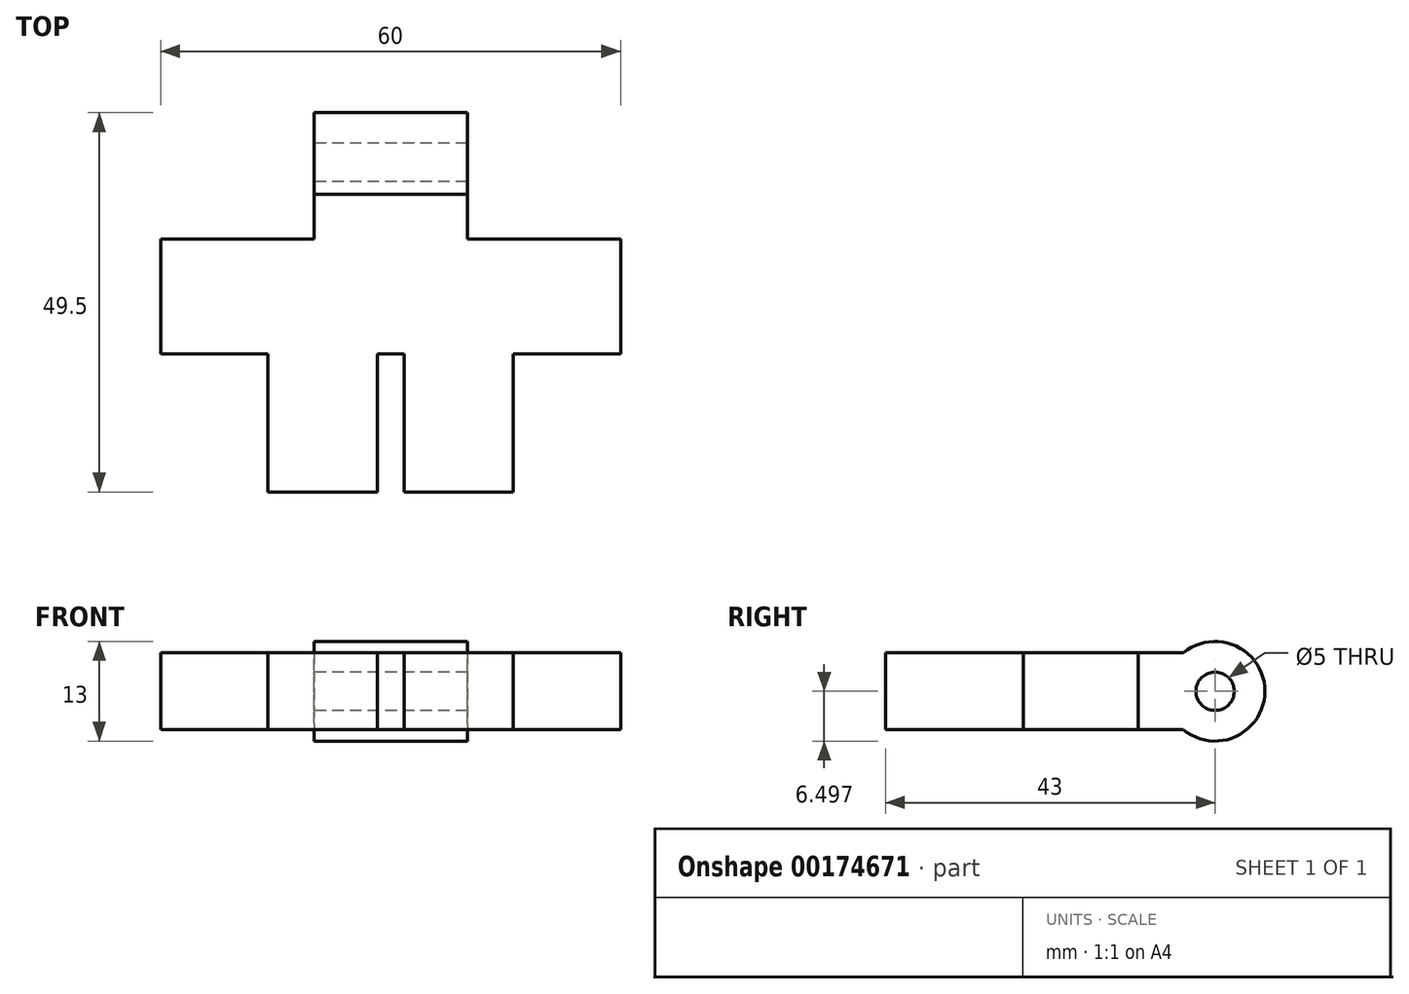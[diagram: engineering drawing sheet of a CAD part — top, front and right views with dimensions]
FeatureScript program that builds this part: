
annotation { "Feature Type Name" : "Feature", "Feature Type Description" : "" }
export const myFeature = defineFeature(function(context is Context, id is Id, definition is map)
    precondition{}
    {
        {
            var Q0;
            Q0=qCreatedBy(makeId("Top.planeOp"),FACE);
            var sketch = newSketch(context, id + "F0", { "sketchPlane" : qUnion([Q0])});
            skLineSegment(sketch, "E0", {"start": v(-30, 0) * mm, "end": v(-30, 15) * mm});
            skLineSegment(sketch, "E1", {"start": v(-30, 0) * mm, "end": v(-16, 0) * mm});
            skLineSegment(sketch, "E2", {"start": v(-16, 0) * mm, "end": v(-16, -18) * mm});
            skLineSegment(sketch, "E3", {"start": v(-16, -18) * mm, "end": v(-1.75, -18) * mm});
            skLineSegment(sketch, "E4", {"start": v(-1.75, -18) * mm, "end": v(-1.75, 0) * mm});
            skLineSegment(sketch, "E5", {"start": v(-1.75, 0) * mm, "end": v(0, 0) * mm});
            skLineSegment(sketch, "E6", {"start": v(-30, 15) * mm, "end": v(-10, 15) * mm});
            skLineSegment(sketch, "E7", {"start": v(-10, 15) * mm, "end": v(-10, 25) * mm});
            skLineSegment(sketch, "E8", {"start": v(-10, 25) * mm, "end": v(0, 25) * mm});
            skLineSegment(sketch, "E9.MirrorCS", {"start": v(10, 25) * mm, "end": v(0, 25) * mm});
            skLineSegment(sketch, "E10.MirrorCS", {"start": v(10, 15) * mm, "end": v(10, 25) * mm});
            skLineSegment(sketch, "E11.MirrorCS", {"start": v(30, 15) * mm, "end": v(10, 15) * mm});
            skLineSegment(sketch, "E12.MirrorCS", {"start": v(30, 0) * mm, "end": v(30, 15) * mm});
            skLineSegment(sketch, "E13.MirrorCS", {"start": v(30, 0) * mm, "end": v(16, 0) * mm});
            skLineSegment(sketch, "E14.MirrorCS", {"start": v(16, 0) * mm, "end": v(16, -18) * mm});
            skLineSegment(sketch, "E15.MirrorCS", {"start": v(16, -18) * mm, "end": v(1.75, -18) * mm});
            skLineSegment(sketch, "E16.MirrorCS", {"start": v(1.75, -18) * mm, "end": v(1.75, 0) * mm});
            skLineSegment(sketch, "E17.MirrorCS", {"start": v(1.75, 0) * mm, "end": v(0, 0) * mm});
            skSolve(sketch);
        }
        {
            var Q0;
            Q0 = qSketchRegion(id + "F0", true);
            extrude(context, id + "F1", {"entities" : qUnion([Q0]), "depth" : 10 * mm});
        }
        {
            var Q0;
            Q0=qCreatedBy(makeId("Right.planeOp"),FACE);
            var sketch = newSketch(context, id + "F2", { "sketchPlane" : qUnion([Q0])});
            skCircle(sketch, "E18", {"center": v(25, 5) * mm, "radius": 6.5 * mm});
            skCircle(sketch, "E19", {"center": v(25, 5) * mm, "radius": 2.5 * mm});
            skSolve(sketch);
        }
        {
            var Q0;
            Q0 = qSketchRegion(id + "F2", true);
            extrude(context, id + "F3", {"entities" : qUnion([Q0]), "operationType" : NewBodyOperationType.ADD, "depth" : 20 * mm, "symmetric" : true});
        }
        {
            var Q0;
            Q0=makeQuery(id+"F2.imprint","IMPRINT",FACE,{"disambiguationData":[TD([[makeQuery(id+"F2.imprint","IMPRINT",EDGE,{"derivedFrom":sQuery(id+"F2.wireOp",EDGE,"E19")}),1.0]])]});
            extrude(context, id + "F4", {"entities" : qUnion([Q0]), "operationType" : NewBodyOperationType.REMOVE, "oppositeDirection" : true, "depth" : 25 * mm, "symmetric" : true});
        }
    });
